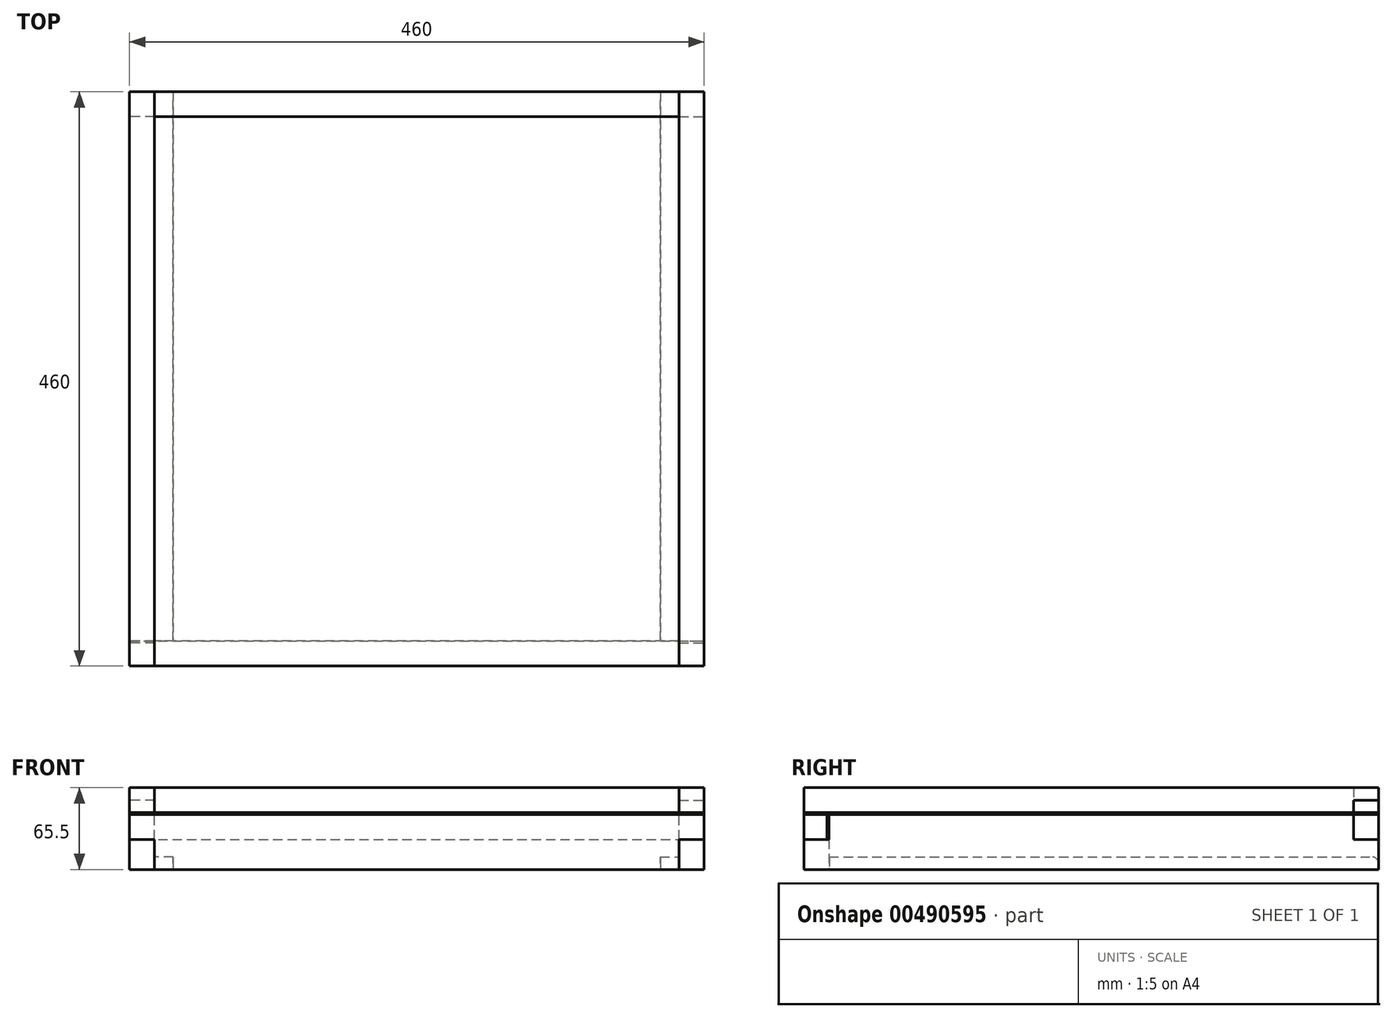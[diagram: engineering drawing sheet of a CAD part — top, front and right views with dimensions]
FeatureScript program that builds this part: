
annotation { "Feature Type Name" : "Feature", "Feature Type Description" : "" }
export const myFeature = defineFeature(function(context is Context, id is Id, definition is map)
    precondition{}
    {
        {
            var Q0;
            Q0=qCreatedBy(makeId("Top.planeOp"),FACE);
            var sketch = newSketch(context, id + "F0", { "sketchPlane" : qUnion([Q0])});
            skLineSegment(sketch, "E0.bottom", {"start": v(0, 0) * mm, "end": v(460, 0) * mm});
            skLineSegment(sketch, "E0.top", {"start": v(0, -460) * mm, "end": v(460, -460) * mm});
            skLineSegment(sketch, "E0.left", {"start": v(0, 0) * mm, "end": v(0, -460) * mm});
            skLineSegment(sketch, "E0.right", {"start": v(460, 0) * mm, "end": v(460, -460) * mm});
            skSolve(sketch);
        }
        {
            var Q0;
            Q0 = qSketchRegion(id + "F0", true);
            extrude(context, id + "F1", {"entities" : qUnion([Q0]), "depth" : 1.5 * mm});
        }
        {
            var Q0;
            Q0=qCreatedBy(makeId("Front.planeOp"),FACE);
            var sketch = newSketch(context, id + "F2", { "sketchPlane" : qUnion([Q0])});
            skLineSegment(sketch, "E1.0", {"start": v(0, 1.5) * mm, "end": v(460, 1.5) * mm});
            skLineSegment(sketch, "E2", {"start": v(0, 1.5) * mm, "end": v(0, 11.5) * mm});
            skLineSegment(sketch, "E3", {"start": v(0, 11.5) * mm, "end": v(20, 11.5) * mm});
            skLineSegment(sketch, "E4", {"start": v(20, 11.5) * mm, "end": v(20, 21.5) * mm});
            skLineSegment(sketch, "E5", {"start": v(20, 21.5) * mm, "end": v(440, 21.5) * mm});
            skLineSegment(sketch, "E6", {"start": v(440, 21.5) * mm, "end": v(440, 11.5) * mm});
            skLineSegment(sketch, "E7", {"start": v(440, 11.5) * mm, "end": v(460, 11.5) * mm});
            skLineSegment(sketch, "E8", {"start": v(460, 1.5) * mm, "end": v(460, 11.5) * mm});
            skSolve(sketch);
        }
        {
            var Q0;
            Q0 = qSketchRegion(id + "F2", true);
            extrude(context, id + "F3", {"entities" : qUnion([Q0]), "depth" : 20 * mm});
        }
        {
            var Q0;
            Q0=makeQuery(id+"F3.opExtrude","SWEPT_FACE",FACE,{"disambiguationData":[OSD([sQuery(id+"F2.wireOp",EDGE,"E2")])]});
            var sketch = newSketch(context, id + "F4", { "sketchPlane" : qUnion([Q0])});
            skLineSegment(sketch, "E9.0", {"start": v(20, 1.5) * mm, "end": v(460, 1.5) * mm});
            skLineSegment(sketch, "E10", {"start": v(460, 1.5) * mm, "end": v(460, 21.5) * mm});
            skLineSegment(sketch, "E11.0", {"start": v(0, 11.5) * mm, "end": v(0, 21.5) * mm});
            skLineSegment(sketch, "E11.1", {"start": v(20, 11.5) * mm, "end": v(0, 11.5) * mm});
            skLineSegment(sketch, "E11.2", {"start": v(20, 1.5) * mm, "end": v(20, 11.5) * mm});
            skLineSegment(sketch, "E11.3", {"start": v(460, 21.5) * mm, "end": v(0, 21.5) * mm});
            skPoint(sketch, "E12.orphan", {"position": v(0, 1.5) * mm});
            skPoint(sketch, "E13.orphan", {"position": v(20, 21.5) * mm});
            skSolve(sketch);
        }
        {
            var Q0;
            Q0 = qSketchRegion(id + "F4", true);
            extrude(context, id + "F5", {"entities" : qUnion([Q0]), "oppositeDirection" : true, "depth" : 20 * mm});
        }
        {
            var Q0;
            Q0=makeQuery(id+"F3.opExtrude","SWEPT_FACE",FACE,{"disambiguationData":[OSD([sQuery(id+"F2.wireOp",EDGE,"E8")])]});
            var sketch = newSketch(context, id + "F6", { "sketchPlane" : qUnion([Q0])});
            skLineSegment(sketch, "E14.0", {"start": v(-20, 1.5) * mm, "end": v(-460, 1.5) * mm});
            skLineSegment(sketch, "E14.1", {"start": v(-460, 1.5) * mm, "end": v(-460, 21.5) * mm});
            skLineSegment(sketch, "E14.2", {"start": v(0, 11.5) * mm, "end": v(0, 21.5) * mm});
            skLineSegment(sketch, "E14.3", {"start": v(-20, 11.5) * mm, "end": v(0, 11.5) * mm});
            skLineSegment(sketch, "E14.4", {"start": v(-20, 1.5) * mm, "end": v(-20, 11.5) * mm});
            skLineSegment(sketch, "E14.5", {"start": v(-460, 21.5) * mm, "end": v(0, 21.5) * mm});
            skPoint(sketch, "E14.6", {"position": v(0, 1.5) * mm});
            skPoint(sketch, "E14.7", {"position": v(-20, 21.5) * mm});
            skSolve(sketch);
        }
        {
            var Q0;
            Q0 = qSketchRegion(id + "F6", true);
            extrude(context, id + "F7", {"entities" : qUnion([Q0]), "oppositeDirection" : true, "depth" : 20 * mm});
        }
        {
            var Q0;
            Q0=makeQuery(id+"F1.opExtrude","CAP_FACE",FACE,{"disambiguationData":[OSD([sQuery(id+"F0.wireOp",EDGE,"E0.bottom"),sQuery(id+"F0.wireOp",EDGE,"E0.top"),sQuery(id+"F0.wireOp",EDGE,"E0.left"),sQuery(id+"F0.wireOp",EDGE,"E0.right")])],"isStart":true});
            var sketch = newSketch(context, id + "F8", { "sketchPlane" : qUnion([Q0])});
            skLineSegment(sketch, "E15.0", {"start": v(0, 20) * mm, "end": v(460, 20) * mm});
            skLineSegment(sketch, "E15.1", {"start": v(0, 0) * mm, "end": v(460, 0) * mm});
            skLineSegment(sketch, "E16", {"start": v(460, 20) * mm, "end": v(460, 0) * mm});
            skLineSegment(sketch, "E17", {"start": v(0, 20) * mm, "end": v(0, 0) * mm});
            skSolve(sketch);
        }
        {
            var Q0;
            Q0 = qSketchRegion(id + "F8", true);
            extrude(context, id + "F9", {"entities" : qUnion([Q0]), "depth" : 20 * mm});
        }
        {
            var Q0;
            Q0=makeQuery(id+"F9.opExtrude","SWEPT_FACE",FACE,{"disambiguationData":[OSD([sQuery(id+"F8.wireOp",EDGE,"E17")])]});
            var sketch = newSketch(context, id + "F10", { "sketchPlane" : qUnion([Q0])});
            skLineSegment(sketch, "E18.0", {"start": v(20, -20) * mm, "end": v(20, 0) * mm});
            skLineSegment(sketch, "E18.1", {"start": v(0, -20) * mm, "end": v(20, -20) * mm});
            skLineSegment(sketch, "E19", {"start": v(0, -20) * mm, "end": v(0, -44) * mm});
            skLineSegment(sketch, "E20", {"start": v(0, -44) * mm, "end": v(460, -44) * mm});
            skLineSegment(sketch, "E21", {"start": v(20, 0) * mm, "end": v(441.56, 0) * mm});
            skLineSegment(sketch, "E22", {"start": v(460, -20) * mm, "end": v(460, -44) * mm});
            skPoint(sketch, "E23.0.start.orphan", {"position": v(460, 1.5) * mm});
            skLineSegment(sketch, "E24", {"start": v(460, -20) * mm, "end": v(441.56, -20) * mm});
            skLineSegment(sketch, "E25", {"start": v(441.56, -20) * mm, "end": v(441.56, 0) * mm});
            skPoint(sketch, "E26.orphan", {"position": v(460, 0) * mm});
            skSolve(sketch);
        }
        {
            var Q0;
            Q0 = qSketchRegion(id + "F10", true);
            extrude(context, id + "F11", {"entities" : qUnion([Q0]), "oppositeDirection" : true, "depth" : 20 * mm});
        }
        {
            var Q0;
            Q0=makeQuery(id+"F9.opExtrude","SWEPT_FACE",FACE,{"disambiguationData":[OSD([sQuery(id+"F8.wireOp",EDGE,"E16")])]});
            var sketch = newSketch(context, id + "F12", { "sketchPlane" : qUnion([Q0])});
            skLineSegment(sketch, "E27.0", {"start": v(-20, -20) * mm, "end": v(-20, 0) * mm});
            skLineSegment(sketch, "E27.1", {"start": v(0, -20) * mm, "end": v(-20, -20) * mm});
            skLineSegment(sketch, "E27.2", {"start": v(0, -20) * mm, "end": v(0, -44) * mm});
            skLineSegment(sketch, "E27.3", {"start": v(0, -44) * mm, "end": v(-460, -44) * mm});
            skLineSegment(sketch, "E27.4", {"start": v(-20, 0) * mm, "end": v(-441.56, 0) * mm});
            skLineSegment(sketch, "E27.5", {"start": v(-460, -20) * mm, "end": v(-460, -44) * mm});
            skPoint(sketch, "E27.6", {"position": v(-460, 1.5) * mm});
            skLineSegment(sketch, "E27.7", {"start": v(-460, -20) * mm, "end": v(-441.56, -20) * mm});
            skLineSegment(sketch, "E27.8", {"start": v(-441.56, -20) * mm, "end": v(-441.56, 0) * mm});
            skPoint(sketch, "E27.9", {"position": v(-460, 0) * mm});
            skSolve(sketch);
        }
        {
            var Q0;
            Q0 = qSketchRegion(id + "F12", true);
            extrude(context, id + "F13", {"entities" : qUnion([Q0]), "oppositeDirection" : true, "depth" : 20 * mm});
        }
        {
            var Q0;
            Q0=makeQuery(id+"F11.opExtrude","SWEPT_FACE",FACE,{"disambiguationData":[OSD([sQuery(id+"F10.wireOp",EDGE,"E22")])]});
            var sketch = newSketch(context, id + "F14", { "sketchPlane" : qUnion([Q0])});
            skLineSegment(sketch, "E28.0", {"start": v(20, -20) * mm, "end": v(0, -20) * mm});
            skLineSegment(sketch, "E28.1", {"start": v(0, -20) * mm, "end": v(0, 0) * mm});
            skLineSegment(sketch, "E28.2", {"start": v(20, -20) * mm, "end": v(20, -44) * mm});
            skLineSegment(sketch, "E28.3", {"start": v(440, -20) * mm, "end": v(440, -44) * mm});
            skLineSegment(sketch, "E28.4", {"start": v(440, -20) * mm, "end": v(460, -20) * mm});
            skLineSegment(sketch, "E28.5", {"start": v(460, -20) * mm, "end": v(460, 0) * mm});
            skLineSegment(sketch, "E29", {"start": v(440, -44) * mm, "end": v(20, -44) * mm});
            skLineSegment(sketch, "E30", {"start": v(0, 0) * mm, "end": v(460, 0) * mm});
            skSolve(sketch);
        }
        {
            var Q0;
            Q0 = qSketchRegion(id + "F14", true);
            extrude(context, id + "F15", {"entities" : qUnion([Q0]), "oppositeDirection" : true, "depth" : 20 * mm});
        }
        {
            var Q0;
            Q0=makeQuery(id+"F15.opExtrude","CAP_EDGE",EDGE,{"disambiguationData":[OSD([sQuery(id+"F14.wireOp",EDGE,"E29")])],"isStart":false});
            cPoint(context, id + "F16", {"entities" : qUnion([Q0]), "parameter" : 0.5});
        }
        {
            var Q0;
            Q0=qCreatedBy(makeId("Right.planeOp"),FACE);
            var Q1;
            Q1 = qCreatedBy(id + "F16" ,VERTEX);
            cPlane(context, id + "F17", {"entities" : qUnion([Q0, Q1]), "cplaneType" : CPlaneType.PLANE_POINT, "offset" : 25 * mm, "width" : 150 * mm, "height" : 150 * mm});
        }
        {
            var Q0;
            Q0=makeQuery(id+"F11.opExtrude","CAP_FACE",FACE,{"disambiguationData":[OSD([sQuery(id+"F10.wireOp",EDGE,"E18.0"),sQuery(id+"F10.wireOp",EDGE,"E18.1"),sQuery(id+"F10.wireOp",EDGE,"E19"),sQuery(id+"F10.wireOp",EDGE,"E20"),sQuery(id+"F10.wireOp",EDGE,"E21"),sQuery(id+"F10.wireOp",EDGE,"E22"),sQuery(id+"F10.wireOp",EDGE,"E24"),sQuery(id+"F10.wireOp",EDGE,"E25")])],"isStart":false});
            var sketch = newSketch(context, id + "F18", { "sketchPlane" : qUnion([Q0])});
            skLineSegment(sketch, "E31.0", {"start": v(0, -44) * mm, "end": v(-439.78, -44) * mm});
            skLineSegment(sketch, "E32", {"start": v(-439.78, -34) * mm, "end": v(-5, -34) * mm});
            skLineSegment(sketch, "E33", {"start": v(0, -39) * mm, "end": v(0, -44) * mm});
            skLineSegment(sketch, "E34", {"start": v(-439.78, -34) * mm, "end": v(-439.78, -44) * mm});
            skPoint(sketch, "E35.orphan", {"position": v(-460, -44) * mm});
            skPoint(sketch, "E36.visualSharp", {"position": v(0, -34) * mm});
            skArc(sketch, "E36.filletArc", {"start": v(0, -39) * mm, "mid": v(-1.46, -35.46) * mm, "end": v(-5, -34) * mm});
            skSolve(sketch);
        }
        {
            var Q0;
            Q0 = qSketchRegion(id + "F18", true);
            extrude(context, id + "F19", {"entities" : qUnion([Q0]), "depth" : 15 * mm});
        }
        {
            var Q0;
            Q0=makeQuery(id+"F19.opExtrude","SWEPT_BODY",BODY,{"disambiguationData":[OSD([sQuery(id+"F18.wireOp",EDGE,"E31.0"),sQuery(id+"F18.wireOp",EDGE,"E32"),sQuery(id+"F18.wireOp",EDGE,"E33"),sQuery(id+"F18.wireOp",EDGE,"E34"),sQuery(id+"F18.wireOp",EDGE,"E36.filletArc")])]});
            var Q1;
            Q1=qCreatedBy(id+"F17.planeOp",FACE);
            mirror(context, id + "F20", {"operationType" : NewBodyOperationType.ADD, "entities" : qUnion([Q0]), "mirrorPlane" : qUnion([Q1])});
        }
    });
